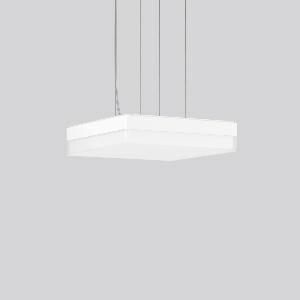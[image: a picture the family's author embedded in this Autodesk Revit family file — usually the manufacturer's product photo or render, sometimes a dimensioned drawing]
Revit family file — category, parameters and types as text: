
# Revit family: flat_slim_square_312541_002_730_d66b
name_source: partatom
category: Lighting Fixtures
units: mm (PartAtom-declared; Revit-internal decimal feet)

## family parameters
Cut with Voids When Loaded = No
Host = Face
Light Source = No
Part Type = Normal
Room Calculation Point = No
Round Connector Dimension = Use Diameter
Shared = No

## types (1)
- MultiLumen 2 840 (1 x LED Modul 840, 2400 lm, 4000)
    Apparent Load = 21 VA
    CIE Flux Codes = 43 74 93 92 100
    Color Rendering = 80
    Color Temperature = 4000
    Default Elevation = 1800 mm
    Height = 70 mm
    Lamp = 1 x LED Modul 840
    Lamp Light Flux = 2400 lm
    Lamp count = 1
    Length = 300 mm
    Lifetime = 50000 h
    Luminous efficacy = 114 lm/W
    Manufacturer = RZB
    ModVariant = No
    Model = 312541.002.730
    Mounting Place = Ceiling
    Mounting Type = Pendant
    Number of Poles = 1
    OnlyDefault = Yes
    Power Factor = 1
    Product Name = FLAT SLIM square
    Product group = Pendant luminaires
    ProductGroupID = 902
    Protection Class = Protection class I
    Protection Degree = IP 40
    RLX_Detail_Level = 1
    RLX_Emergency_Light_Flux = 0 lm
    RLX_Emergency_Type = 0
    RLX_Emergency_Type_DB = No
    RlxData = <blob elided: 14421 chars, md5=2280bdfa>
    Socket = socket
    Standby Power = 0 W
    System Light Flux = 2400 lm
    System Power = 21 W
    Type Comments = MultiLumen 2 840
    Type Image = 312541.002.jpg
    URL = http://relux.com
    VarID = multilumen_2_840
    Voltage = 230 V
    Voltage Range = 220-240 V
    Weight = 0.00 kg
    Width = 300 mm

## geometry (parser evidence)
native form markers: Sweep x14
no freeform markers — native parametric forms only
